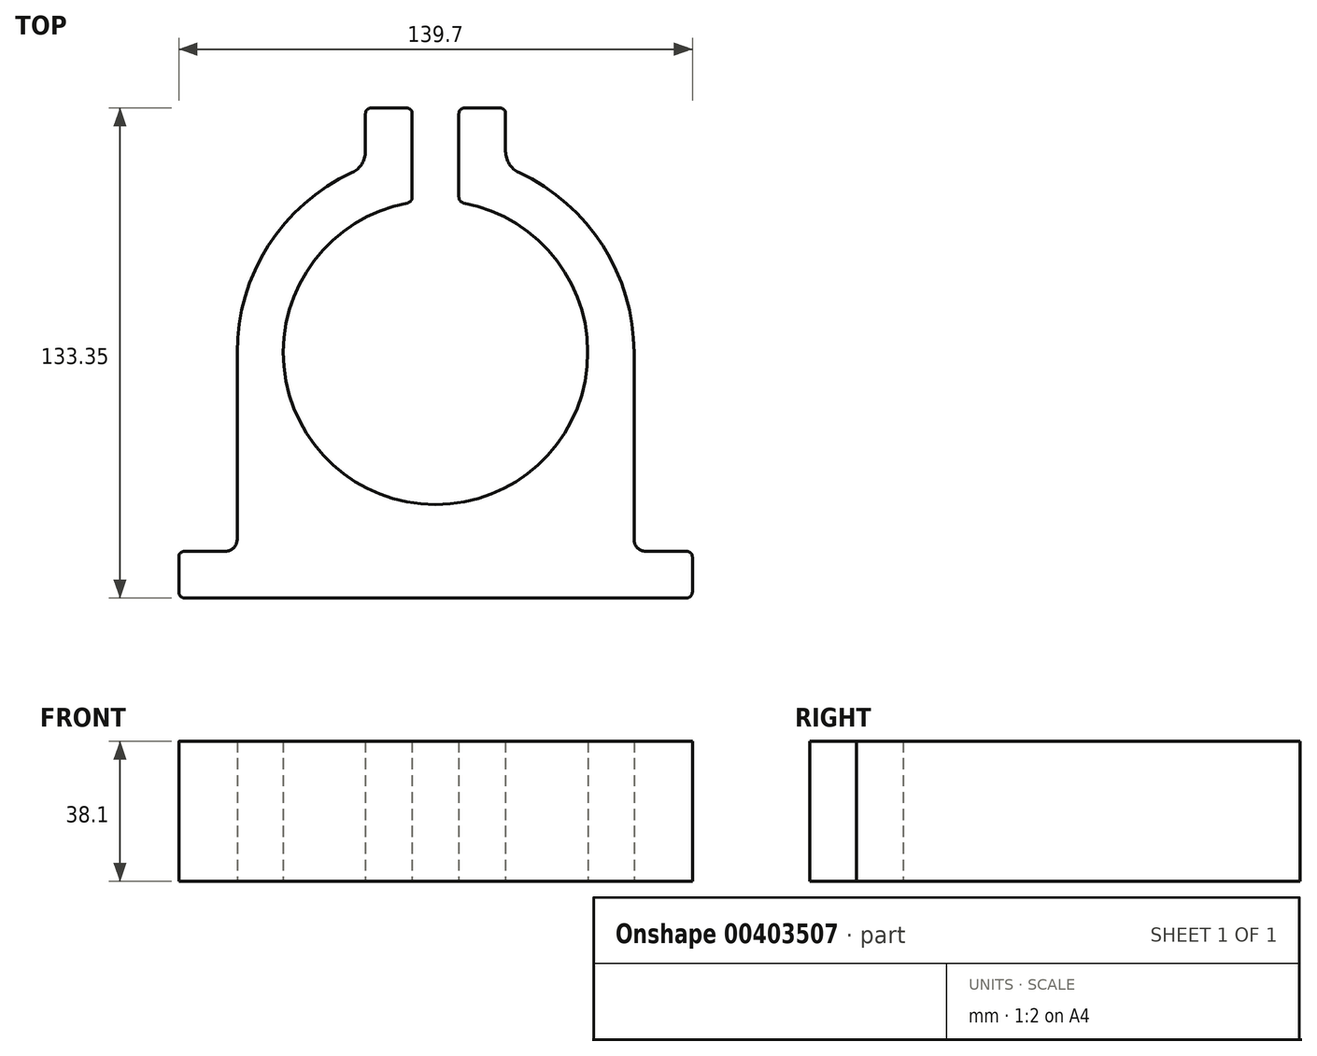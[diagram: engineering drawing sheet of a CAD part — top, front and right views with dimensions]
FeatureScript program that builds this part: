
annotation { "Feature Type Name" : "Feature", "Feature Type Description" : "" }
export const myFeature = defineFeature(function(context is Context, id is Id, definition is map)
    precondition{}
    {
        {
            var Q0;
            Q0=qCreatedBy(makeId("Top.planeOp"),FACE);
            var sketch = newSketch(context, id + "F0", { "sketchPlane" : qUnion([Q0])});
            skLineSegment(sketch, "E0", {"start": v(1.59, 0) * mm, "end": v(138.11, 0) * mm});
            skLineSegment(sketch, "E1", {"start": v(139.7, 1.59) * mm, "end": v(139.7, 11.11) * mm});
            skLineSegment(sketch, "E2", {"start": v(138.11, 12.7) * mm, "end": v(127, 12.7) * mm});
            skLineSegment(sketch, "E3", {"start": v(123.83, 15.88) * mm, "end": v(123.83, 66.8) * mm});
            skLineSegment(sketch, "E4", {"start": v(15.88, 66.8) * mm, "end": v(15.88, 15.88) * mm});
            skLineSegment(sketch, "E5", {"start": v(12.7, 12.7) * mm, "end": v(1.59, 12.7) * mm});
            skLineSegment(sketch, "E6", {"start": v(0, 11.11) * mm, "end": v(0, 1.59) * mm});
            skArc(sketch, "E7", {"start": v(123.83, 66.8) * mm, "mid": v(115.35, 95.84) * mm, "end": v(92.58, 115.76) * mm});
            skPoint(sketch, "E7.startSnap0", {"position": v(69.85, 66.8) * mm});
            skLineSegment(sketch, "E8.trimOffspring", {"start": v(123.83, 66.8) * mm, "end": v(123.83, 66.8) * mm});
            skPoint(sketch, "E9.orphan", {"position": v(69.85, 120.78) * mm});
            skArc(sketch, "E10", {"start": v(62.2, 107.5) * mm, "mid": v(69.85, 25.4) * mm, "end": v(77.5, 107.5) * mm});
            skLineSegment(sketch, "E11", {"start": v(63.5, 109.05) * mm, "end": v(63.5, 131.76) * mm});
            skLineSegment(sketch, "E12", {"start": v(61.91, 133.35) * mm, "end": v(52.39, 133.35) * mm});
            skLineSegment(sketch, "E13", {"start": v(50.8, 131.76) * mm, "end": v(50.8, 121.52) * mm});
            skLineSegment(sketch, "E14", {"start": v(69.85, 66.8) * mm, "end": v(69.85, 128.19) * mm, "construction": true});
            skLineSegment(sketch, "E15.MirrorCS", {"start": v(76.2, 109.05) * mm, "end": v(76.2, 131.76) * mm});
            skLineSegment(sketch, "E16.MirrorCS", {"start": v(77.79, 133.35) * mm, "end": v(87.31, 133.35) * mm});
            skLineSegment(sketch, "E17.MirrorCS", {"start": v(88.9, 131.76) * mm, "end": v(88.9, 121.52) * mm});
            skArc(sketch, "E18.trimOffspring", {"start": v(47.12, 115.76) * mm, "mid": v(24.35, 95.84) * mm, "end": v(15.88, 66.8) * mm});
            skLineSegment(sketch, "E19", {"start": v(69.85, 0) * mm, "end": v(69.85, 37.1) * mm, "construction": true});
            skPoint(sketch, "E20.visualSharp", {"position": v(50.8, 117.3) * mm});
            skArc(sketch, "E20.filletArc", {"start": v(47.12, 115.76) * mm, "mid": v(49.8, 118.1) * mm, "end": v(50.8, 121.52) * mm});
            skPoint(sketch, "E21.visualSharp", {"position": v(88.9, 117.3) * mm});
            skArc(sketch, "E21.filletArc", {"start": v(88.9, 121.52) * mm, "mid": v(89.9, 118.1) * mm, "end": v(92.58, 115.76) * mm});
            skPoint(sketch, "E22.visualSharp", {"position": v(123.83, 12.7) * mm});
            skPoint(sketch, "E23.visualSharp", {"position": v(15.88, 12.7) * mm});
            skArc(sketch, "E24.filletArc", {"start": v(62.2, 107.5) * mm, "mid": v(63.13, 108.04) * mm, "end": v(63.5, 109.05) * mm});
            skPoint(sketch, "E25.visualSharp", {"position": v(139.7, 12.7) * mm});
            skArc(sketch, "E25.filletArc", {"start": v(139.7, 11.11) * mm, "mid": v(139.24, 12.24) * mm, "end": v(138.11, 12.7) * mm});
            skPoint(sketch, "E26.visualSharp", {"position": v(139.7, 0) * mm});
            skArc(sketch, "E26.filletArc", {"start": v(138.11, 0) * mm, "mid": v(139.24, 0.46) * mm, "end": v(139.7, 1.59) * mm});
            skPoint(sketch, "E27.visualSharp", {"position": v(0, 0) * mm});
            skArc(sketch, "E27.filletArc", {"start": v(0, 1.59) * mm, "mid": v(0.46, 0.46) * mm, "end": v(1.59, 0) * mm});
            skPoint(sketch, "E28.visualSharp", {"position": v(0, 12.7) * mm});
            skArc(sketch, "E28.filletArc", {"start": v(1.59, 12.7) * mm, "mid": v(0.46, 12.24) * mm, "end": v(0, 11.11) * mm});
            skPoint(sketch, "E29.visualSharp", {"position": v(76.2, 107.71) * mm});
            skArc(sketch, "E29.filletArc", {"start": v(76.2, 109.05) * mm, "mid": v(76.57, 108.04) * mm, "end": v(77.5, 107.5) * mm});
            skPoint(sketch, "E30.visualSharp", {"position": v(50.8, 133.35) * mm});
            skArc(sketch, "E30.filletArc", {"start": v(52.39, 133.35) * mm, "mid": v(51.26, 132.89) * mm, "end": v(50.8, 131.76) * mm});
            skPoint(sketch, "E31.visualSharp", {"position": v(63.5, 133.35) * mm});
            skArc(sketch, "E31.filletArc", {"start": v(63.5, 131.76) * mm, "mid": v(63.04, 132.89) * mm, "end": v(61.91, 133.35) * mm});
            skPoint(sketch, "E32.visualSharp", {"position": v(88.9, 133.35) * mm});
            skArc(sketch, "E32.filletArc", {"start": v(88.9, 131.76) * mm, "mid": v(88.44, 132.89) * mm, "end": v(87.31, 133.35) * mm});
            skPoint(sketch, "E33.visualSharp", {"position": v(76.2, 133.35) * mm});
            skArc(sketch, "E33.filletArc", {"start": v(77.79, 133.35) * mm, "mid": v(76.66, 132.89) * mm, "end": v(76.2, 131.76) * mm});
            skArc(sketch, "E34.filletArc", {"start": v(12.7, 12.7) * mm, "mid": v(14.95, 13.63) * mm, "end": v(15.88, 15.88) * mm});
            skArc(sketch, "E35.filletArc", {"start": v(123.83, 15.88) * mm, "mid": v(124.75, 13.63) * mm, "end": v(127, 12.7) * mm});
            skSolve(sketch);
        }
        {
            var Q0;
            Q0=qSketchRegion(id+"F0",true);
            extrude(context, id + "F1", {"entities" : qUnion([Q0]), "depth" : 38.1 * mm});
        }
    });
